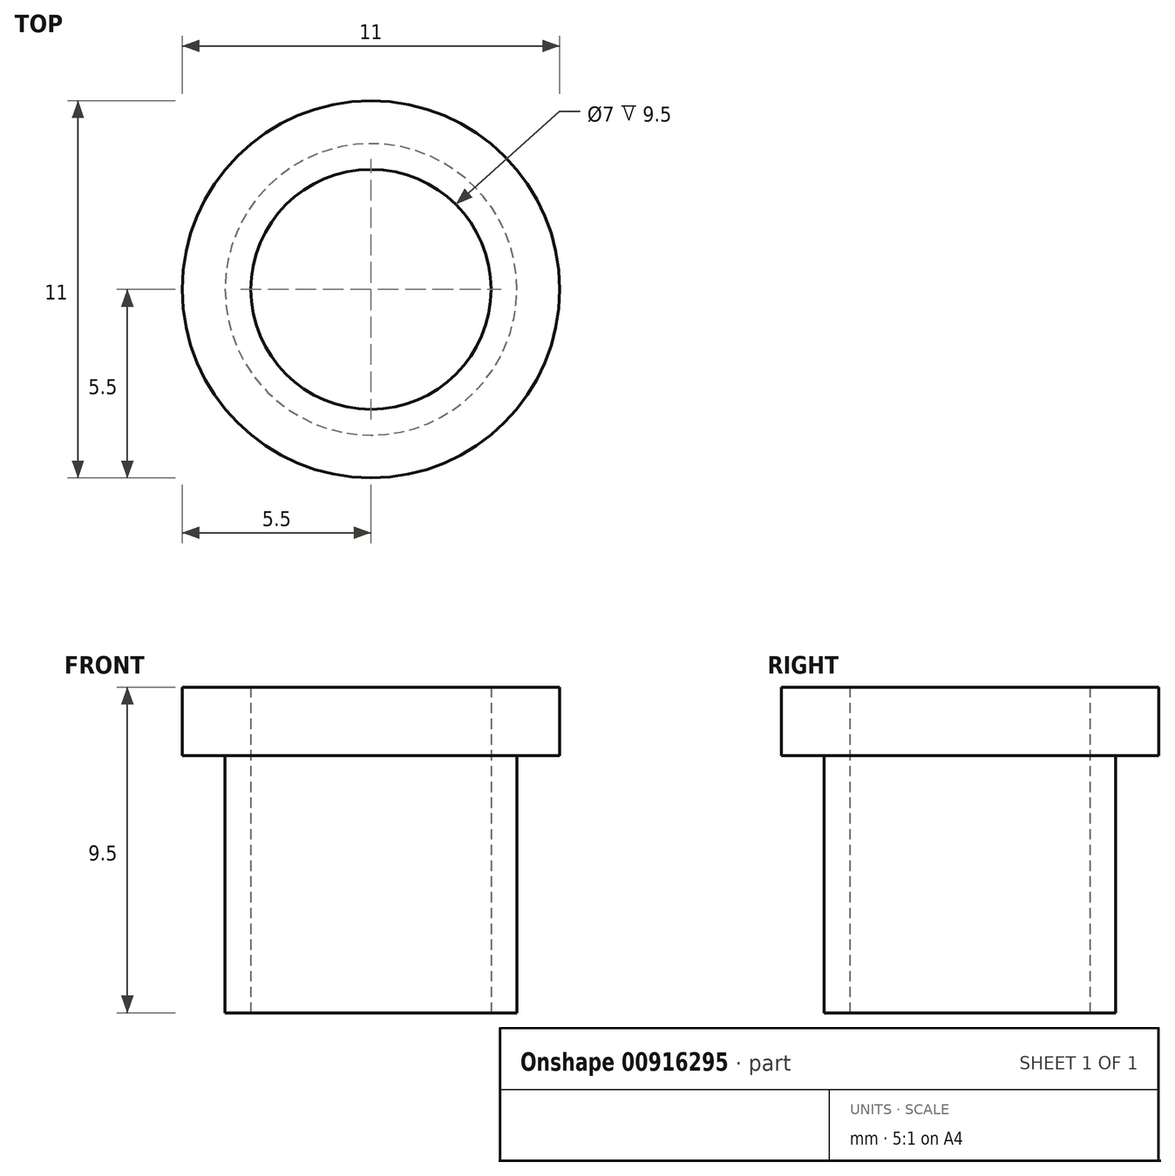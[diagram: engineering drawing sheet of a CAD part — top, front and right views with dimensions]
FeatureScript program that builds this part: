
annotation { "Feature Type Name" : "Feature", "Feature Type Description" : "" }
export const myFeature = defineFeature(function(context is Context, id is Id, definition is map)
    precondition{}
    {
        {
            var Q0;
            Q0=qCreatedBy(makeId("Top.planeOp"),FACE);
            var sketch = newSketch(context, id + "F0", { "sketchPlane" : qUnion([Q0])});
            skCircle(sketch, "E0", {"center": v(0, 0) * mm, "radius": 4.25 * mm});
            skCircle(sketch, "E1", {"center": v(0, 0) * mm, "radius": 5.5 * mm});
            skCircle(sketch, "E2", {"center": v(0, 0) * mm, "radius": 3.5 * mm});
            skSolve(sketch);
        }
        {
            var Q0;
            Q0=makeQuery(id+"F0.imprint","IMPRINT",FACE,{"disambiguationData":[TD([[makeQuery(id+"F0.imprint","IMPRINT",EDGE,{"derivedFrom":sQuery(id+"F0.wireOp",EDGE,"E0")}),1.0]])]});
            var Q1;
            Q1=makeQuery(id+"F0.imprint","IMPRINT",FACE,{"disambiguationData":[TD([[makeQuery(id+"F0.imprint","IMPRINT",EDGE,{"derivedFrom":sQuery(id+"F0.wireOp",EDGE,"E0")}),-1.0]])]});
            var Q2;
            Q2=makeQuery(id+"F0.imprint","IMPRINT",FACE,{"disambiguationData":[TD([[makeQuery(id+"F0.imprint","IMPRINT",EDGE,{"derivedFrom":sQuery(id+"F0.wireOp",EDGE,"E2")}),-1.0]])]});
            var Q3;
            {var subQ0=sQuery(id+"F0.wireOp",EDGE,"c9a7173d-96af-488b-b435-3687b4f67b48.2.0");Q3=makeQuery(id+"F0.imprint","IMPRINT",FACE,{"disambiguationData":[TD([[makeQuery(id+"F0.imprint","IMPRINT",EDGE,{"derivedFrom":subQ0}),1.0]])]});}
            var Q4;
            {var subQ0=sQuery(id+"F0.wireOp",EDGE,"c9a7173d-96af-488b-b435-3687b4f67b48.1.0");Q4=makeQuery(id+"F0.imprint","IMPRINT",FACE,{"disambiguationData":[TD([[makeQuery(id+"F0.imprint","IMPRINT",EDGE,{"derivedFrom":subQ0}),1.0]])]});}
            var Q5;
            {var subQ1=sQuery(id+"F0.wireOp",EDGE,"WYUomJ4n-vd0I-HTI7-DcGG-yMGm0abcDFFH");Q5=makeQuery(id+"F0.imprint","IMPRINT",FACE,{"disambiguationData":[TD([[makeQuery(id+"F0.imprint","IMPRINT",EDGE,{"derivedFrom":subQ1}),-1.0]])]});}
            var Q6;
            {var subQ0=sQuery(id+"F0.wireOp",EDGE,"c9a7173d-96af-488b-b435-3687b4f67b48.7.0");Q6=makeQuery(id+"F0.imprint","IMPRINT",FACE,{"disambiguationData":[TD([[makeQuery(id+"F0.imprint","IMPRINT",EDGE,{"derivedFrom":subQ0}),1.0]])]});}
            var Q7;
            {var subQ0=sQuery(id+"F0.wireOp",EDGE,"c9a7173d-96af-488b-b435-3687b4f67b48.6.0");Q7=makeQuery(id+"F0.imprint","IMPRINT",FACE,{"disambiguationData":[TD([[makeQuery(id+"F0.imprint","IMPRINT",EDGE,{"derivedFrom":subQ0}),1.0]])]});}
            var Q8;
            {var subQ0=sQuery(id+"F0.wireOp",EDGE,"c9a7173d-96af-488b-b435-3687b4f67b48.5.0");Q8=makeQuery(id+"F0.imprint","IMPRINT",FACE,{"disambiguationData":[TD([[makeQuery(id+"F0.imprint","IMPRINT",EDGE,{"derivedFrom":subQ0}),1.0]])]});}
            var Q9;
            {var subQ0=sQuery(id+"F0.wireOp",EDGE,"c9a7173d-96af-488b-b435-3687b4f67b48.4.0");Q9=makeQuery(id+"F0.imprint","IMPRINT",FACE,{"disambiguationData":[TD([[makeQuery(id+"F0.imprint","IMPRINT",EDGE,{"derivedFrom":subQ0}),1.0]])]});}
            var Q10;
            {var subQ0=sQuery(id+"F0.wireOp",EDGE,"c9a7173d-96af-488b-b435-3687b4f67b48.3.0");Q10=makeQuery(id+"F0.imprint","IMPRINT",FACE,{"disambiguationData":[TD([[makeQuery(id+"F0.imprint","IMPRINT",EDGE,{"derivedFrom":subQ0}),1.0]])]});}
            extrude(context, id + "F1", {"entities" : qUnion([Q0, Q1, Q2, Q3, Q4, Q5, Q6, Q7, Q8, Q9, Q10]), "depth" : 2 * mm, "offsetDistance" : 25 * mm});
        }
        {
            var Q0;
            Q0=makeQuery(id+"F0.imprint","IMPRINT",FACE,{"disambiguationData":[TD([[makeQuery(id+"F0.imprint","IMPRINT",EDGE,{"derivedFrom":sQuery(id+"F0.wireOp",EDGE,"E0")}),1.0]])]});
            var Q1;
            Q1=makeQuery(id+"F0.imprint","IMPRINT",FACE,{"disambiguationData":[TD([[makeQuery(id+"F0.imprint","IMPRINT",EDGE,{"derivedFrom":sQuery(id+"F0.wireOp",EDGE,"E2")}),-1.0]])]});
            extrude(context, id + "F2", {"entities" : qUnion([Q0, Q1]), "operationType" : NewBodyOperationType.ADD, "oppositeDirection" : true, "depth" : 7.5 * mm, "offsetDistance" : 25 * mm});
        }
    });
